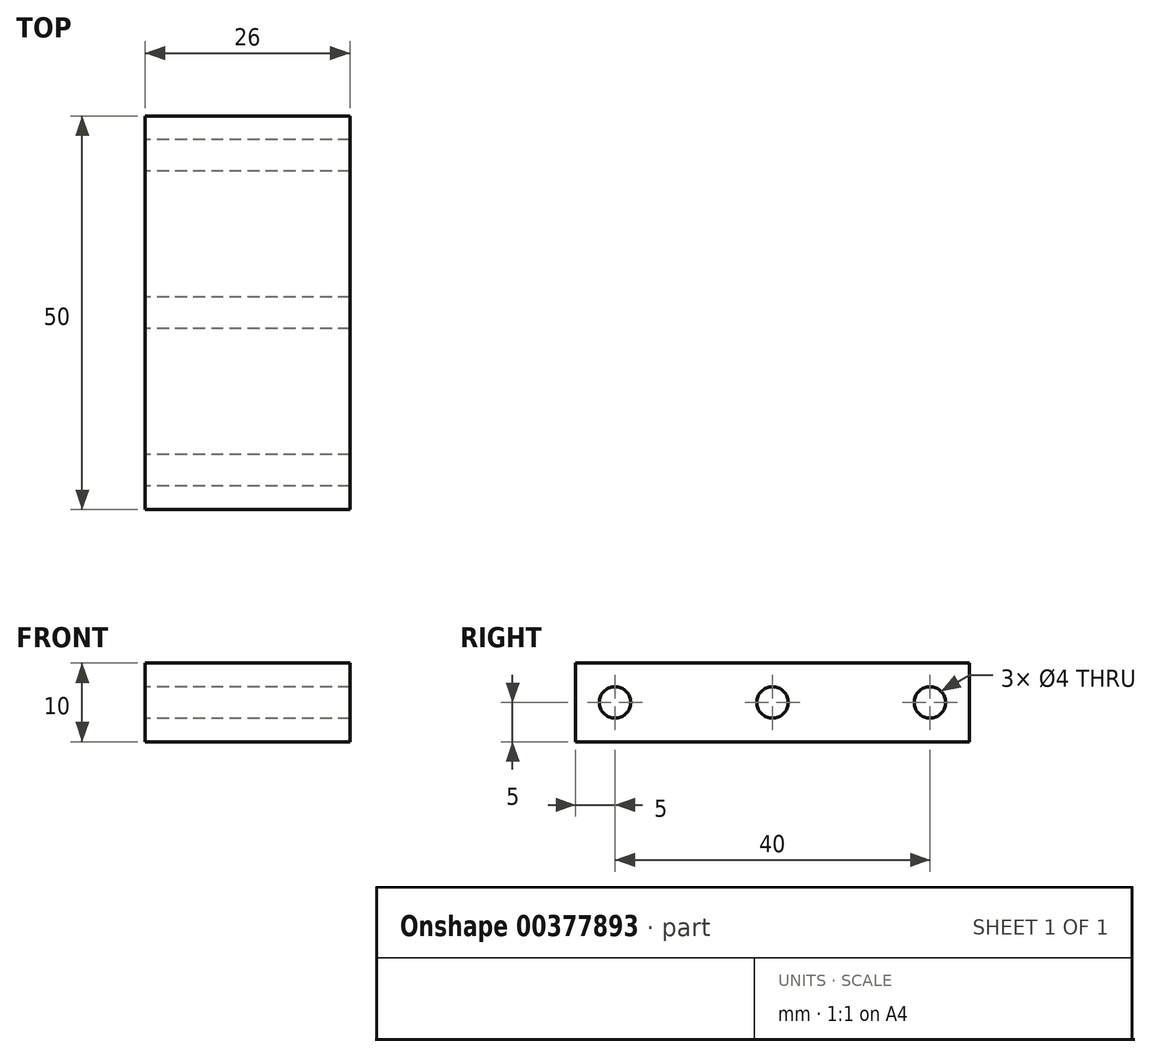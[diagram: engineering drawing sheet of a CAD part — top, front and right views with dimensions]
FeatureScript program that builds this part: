
annotation { "Feature Type Name" : "Feature", "Feature Type Description" : "" }
export const myFeature = defineFeature(function(context is Context, id is Id, definition is map)
    precondition{}
    {
        {
            var Q0;
            Q0=qCreatedBy(makeId("Top.planeOp"),FACE);
            var sketch = newSketch(context, id + "F0", { "sketchPlane" : qUnion([Q0])});
            skLineSegment(sketch, "E0.bottom", {"start": v(-13, 25) * mm, "end": v(13, 25) * mm});
            skLineSegment(sketch, "E0.top", {"start": v(-13, -25) * mm, "end": v(13, -25) * mm});
            skLineSegment(sketch, "E0.left", {"start": v(-13, 25) * mm, "end": v(-13, -25) * mm});
            skLineSegment(sketch, "E0.right", {"start": v(13, 25) * mm, "end": v(13, -25) * mm});
            skPoint(sketch, "E0.middle", {"position": v(0, 0) * mm});
            skSolve(sketch);
        }
        {
            var Q0;
            Q0 = qSketchRegion(id + "F0", true);
            extrude(context, id + "F1", {"entities" : qUnion([Q0]), "depth" : 5 * mm, "hasSecondDirection" : true, "secondDirectionOppositeDirection" : true, "secondDirectionDepth" : 5 * mm});
        }
        {
            var Q0;
            Q0=makeQuery(id+"F1.opExtrude","SWEPT_FACE",FACE,{"disambiguationData":[OSD([sQuery(id+"F0.wireOp",EDGE,"E0.left")])]});
            var sketch = newSketch(context, id + "F2", { "sketchPlane" : qUnion([Q0])});
            skCircle(sketch, "E1", {"center": v(0, 0) * mm, "radius": 2 * mm});
            skCircle(sketch, "E2", {"center": v(20, 0) * mm, "radius": 2 * mm});
            skCircle(sketch, "E3.MirrorC", {"center": v(-20, 0) * mm, "radius": 2 * mm});
            skSolve(sketch);
        }
        {
            var Q0;
            Q0 = qSketchRegion(id + "F2", true);
            extrude(context, id + "F3", {"entities" : qUnion([Q0]), "operationType" : NewBodyOperationType.REMOVE, "endBound" : BoundingType.THROUGH_ALL, "oppositeDirection" : true, "depth" : 25 * mm});
        }
        {
            var Q0;
            Q0 = qSketchRegion(id + "F2", true);
            extrude(context, id + "F4", {"entities" : qUnion([Q0]), "operationType" : NewBodyOperationType.REMOVE, "endBound" : BoundingType.THROUGH_ALL, "oppositeDirection" : true, "depth" : 25 * mm});
        }
    });
